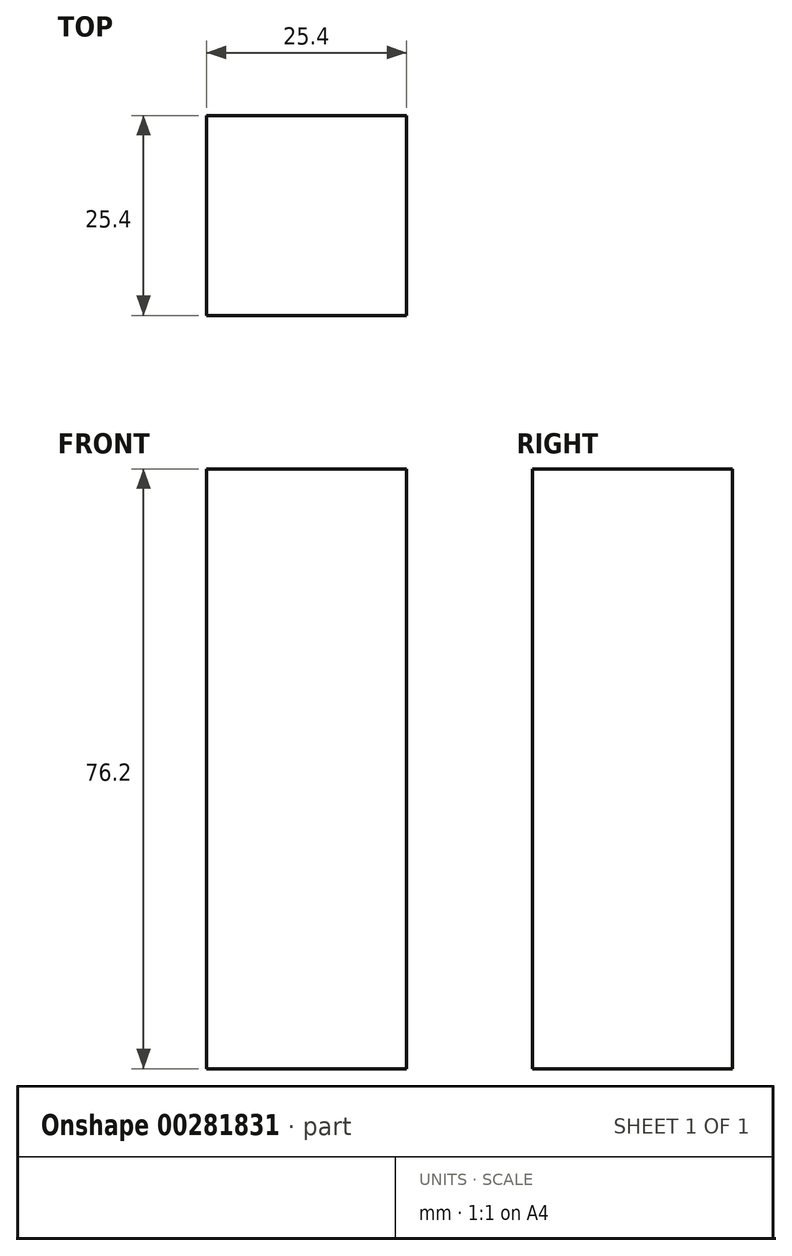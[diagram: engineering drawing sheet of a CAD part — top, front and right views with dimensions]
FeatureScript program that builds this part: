
annotation { "Feature Type Name" : "Feature", "Feature Type Description" : "" }
export const myFeature = defineFeature(function(context is Context, id is Id, definition is map)
    precondition{}
    {
        {
            var Q0;
            Q0=qCreatedBy(makeId("Front.planeOp"),FACE);
            var sketch = newSketch(context, id + "F0", { "sketchPlane" : qUnion([Q0])});
            skLineSegment(sketch, "E0.bottom", {"start": v(0, 0) * mm, "end": v(0, 0) * mm});
            skLineSegment(sketch, "E1", {"start": v(0, 0) * mm, "end": v(0, 76.2) * mm});
            skLineSegment(sketch, "E2", {"start": v(0, 76.2) * mm, "end": v(-25.4, 76.2) * mm});
            skLineSegment(sketch, "E3", {"start": v(-25.4, 76.2) * mm, "end": v(-25.4, 0) * mm});
            skLineSegment(sketch, "E4", {"start": v(-25.4, 0) * mm, "end": v(0, 0) * mm});
            skSolve(sketch);
        }
        {
            var Q0;
            Q0 = qSketchRegion(id + "F0", true);
            extrude(context, id + "F1", {"entities" : qUnion([Q0]), "depth" : 25.4 * mm});
        }
    });
